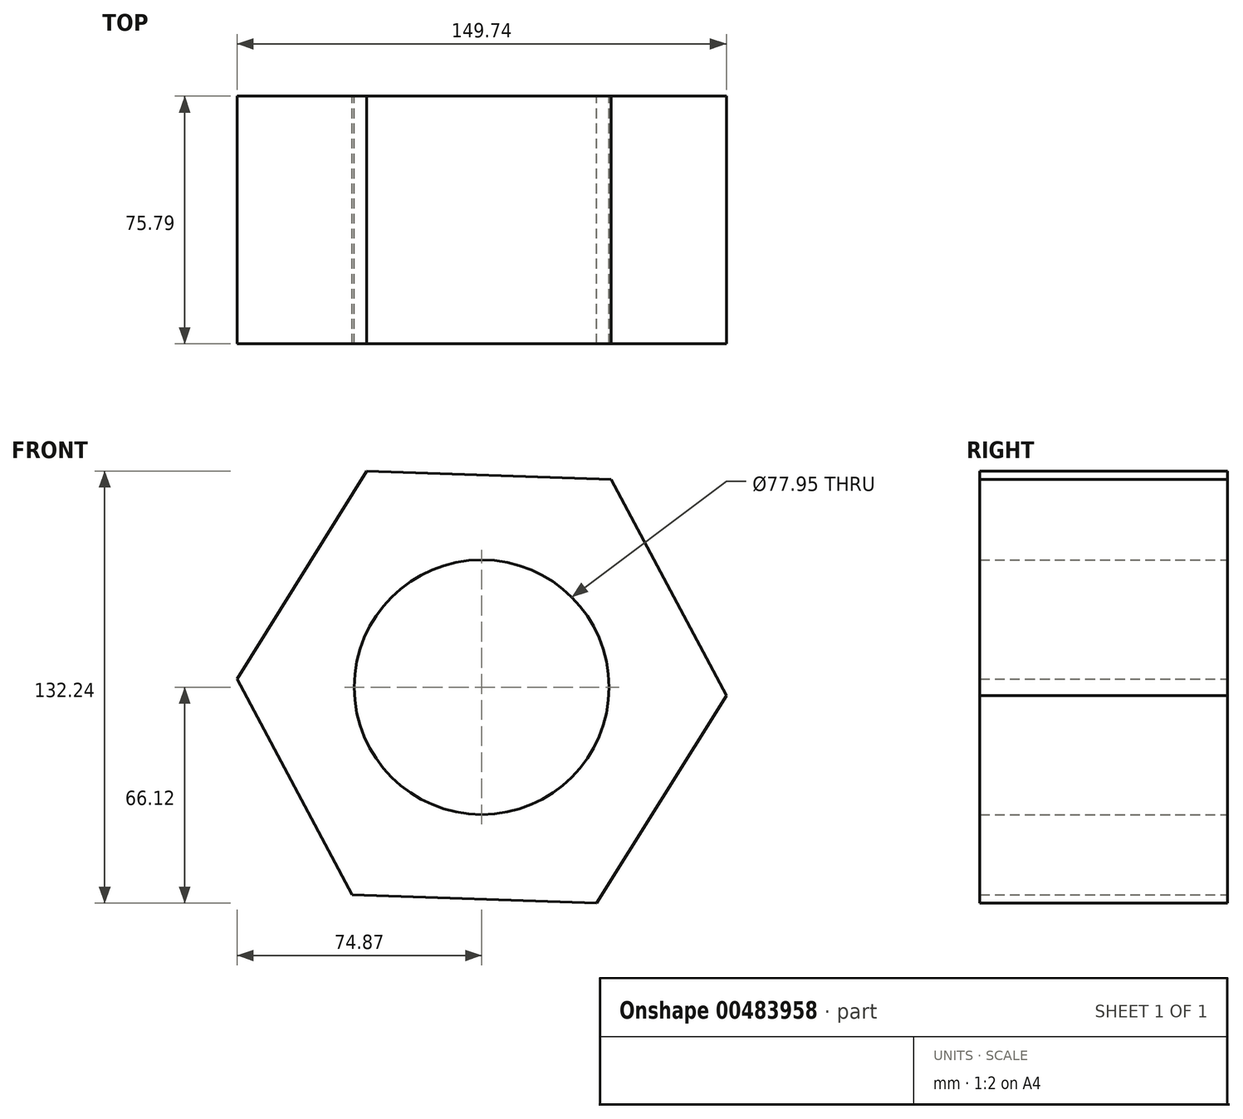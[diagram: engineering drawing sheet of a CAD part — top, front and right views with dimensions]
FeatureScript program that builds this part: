
annotation { "Feature Type Name" : "Feature", "Feature Type Description" : "" }
export const myFeature = defineFeature(function(context is Context, id is Id, definition is map)
    precondition{}
    {
        {
            var Q0;
            Q0=qCreatedBy(makeId("Front.planeOp"),FACE);
            var sketch = newSketch(context, id + "F0", { "sketchPlane" : qUnion([Q0])});
            skCircle(sketch, "E0.cCircle", {"center": v(0, 0) * mm, "radius": 64.87 * mm, "construction": true});
            skLineSegment(sketch, "E0.0", {"start": v(39.65, 63.56) * mm, "end": v(74.87, -2.56) * mm});
            skLineSegment(sketch, "E0.1", {"start": v(74.87, -2.56) * mm, "end": v(35.22, -66.12) * mm});
            skLineSegment(sketch, "E0.2", {"start": v(35.22, -66.12) * mm, "end": v(-39.65, -63.56) * mm});
            skLineSegment(sketch, "E0.3", {"start": v(-39.65, -63.56) * mm, "end": v(-74.87, 2.56) * mm});
            skLineSegment(sketch, "E0.4", {"start": v(-74.87, 2.56) * mm, "end": v(-35.22, 66.12) * mm});
            skLineSegment(sketch, "E0.5", {"start": v(-35.22, 66.12) * mm, "end": v(39.65, 63.56) * mm});
            skPoint(sketch, "E0.0.midPoint", {"position": v(57.26, 30.5) * mm});
            skCircle(sketch, "E1", {"center": v(0, 0) * mm, "radius": 38.98 * mm});
            skSolve(sketch);
        }
        {
            var Q0;
            Q0=makeQuery(id+"F0.imprint","IMPRINT",FACE,{"disambiguationData":[TD([[makeQuery(id+"F0.imprint","IMPRINT",EDGE,{"derivedFrom":sQuery(id+"F0.wireOp",EDGE,"E0.0")}),-1.0]])]});
            extrude(context, id + "F1", {"entities" : qUnion([Q0]), "depth" : 75.8 * mm});
        }
    });
